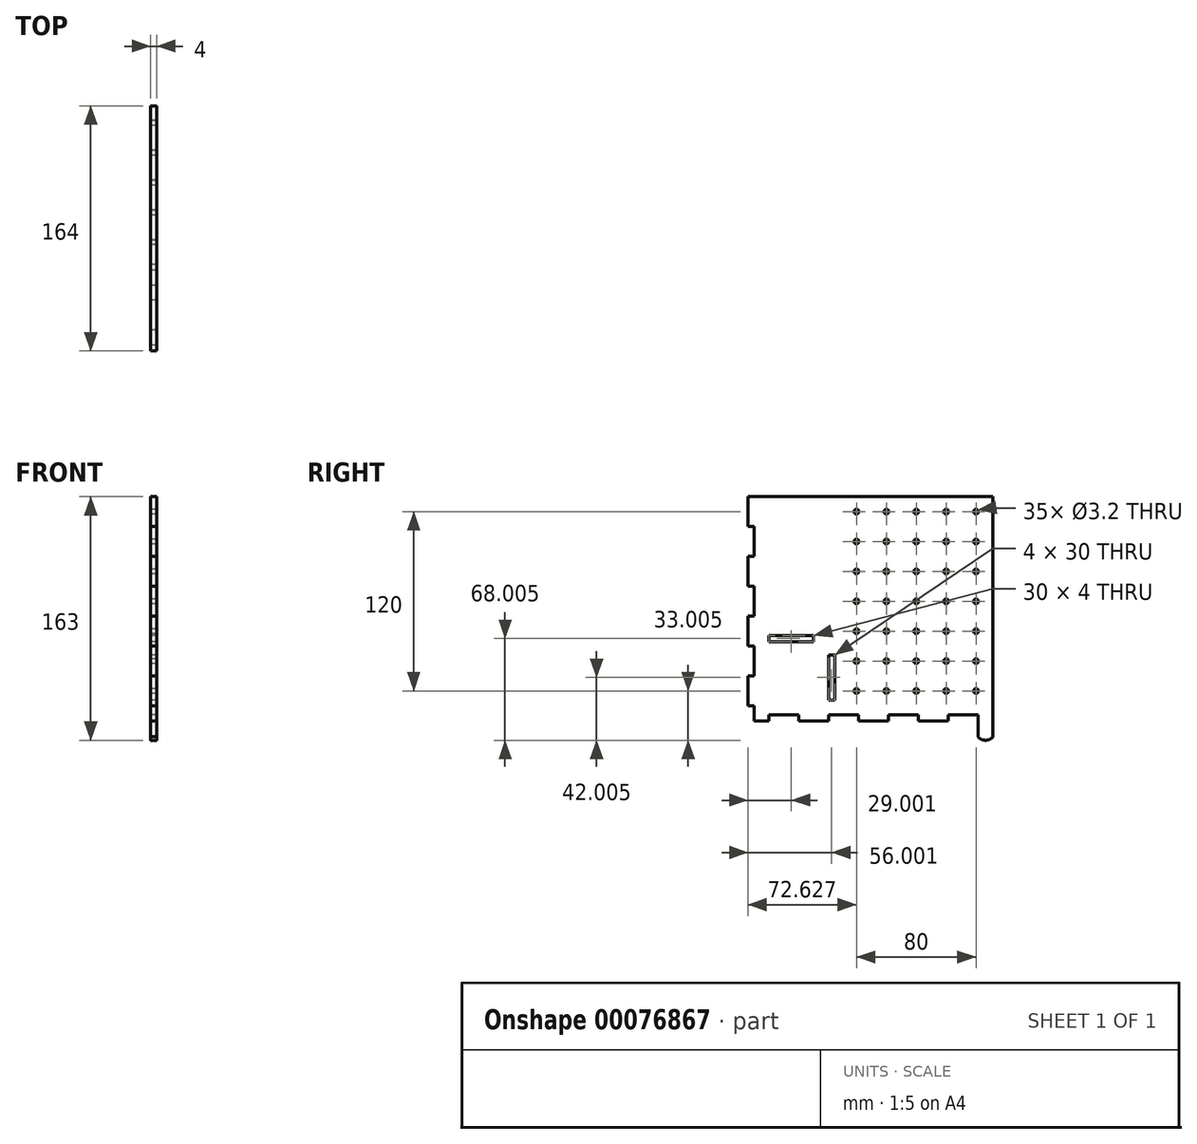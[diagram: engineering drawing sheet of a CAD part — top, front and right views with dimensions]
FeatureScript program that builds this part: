
annotation { "Feature Type Name" : "Feature", "Feature Type Description" : "" }
export const myFeature = defineFeature(function(context is Context, id is Id, definition is map)
    precondition{}
    {
        {
            var Q0;
            Q0=qCreatedBy(makeId("Right.planeOp"),FACE);
            var sketch = newSketch(context, id + "F0", { "sketchPlane" : qUnion([Q0])});
            skLineSegment(sketch, "E0.bottom", {"start": v(-129.98, 84.83) * mm, "end": v(30.02, 84.83) * mm, "construction": true});
            skLineSegment(sketch, "E0.top", {"start": v(-129.98, -65.17) * mm, "end": v(30.02, -65.17) * mm, "construction": true});
            skLineSegment(sketch, "E0.left", {"start": v(-129.98, 84.83) * mm, "end": v(-129.98, -65.17) * mm, "construction": true});
            skLineSegment(sketch, "E0.right", {"start": v(30.02, 84.83) * mm, "end": v(30.02, -65.17) * mm, "construction": true});
            skLineSegment(sketch, "E1.bottom", {"start": v(-119.98, -61.17) * mm, "end": v(-99.98, -61.17) * mm});
            skLineSegment(sketch, "E1.left", {"start": v(-119.98, -61.17) * mm, "end": v(-119.98, -65.17) * mm});
            skLineSegment(sketch, "E1.right", {"start": v(-99.98, -61.17) * mm, "end": v(-99.98, -65.17) * mm});
            skLineSegment(sketch, "E2.1.0.1", {"start": v(-79.98, -61.17) * mm, "end": v(-59.98, -61.17) * mm});
            skLineSegment(sketch, "E2.1.0.2", {"start": v(-79.98, -61.17) * mm, "end": v(-79.98, -65.17) * mm});
            skLineSegment(sketch, "E2.1.0.3", {"start": v(-59.98, -61.17) * mm, "end": v(-59.98, -65.17) * mm});
            skLineSegment(sketch, "E2.2.0.1", {"start": v(-39.98, -61.17) * mm, "end": v(-19.98, -61.17) * mm});
            skLineSegment(sketch, "E2.2.0.2", {"start": v(-39.98, -61.17) * mm, "end": v(-39.98, -65.17) * mm});
            skLineSegment(sketch, "E2.2.0.3", {"start": v(-19.98, -61.17) * mm, "end": v(-19.98, -65.17) * mm});
            skLineSegment(sketch, "E2.3.0.1", {"start": v(0.02, -61.17) * mm, "end": v(20.02, -61.17) * mm});
            skLineSegment(sketch, "E2.3.0.2", {"start": v(0.02, -61.17) * mm, "end": v(0.02, -65.17) * mm});
            skLineSegment(sketch, "E2.3.0.3", {"start": v(20.02, -61.17) * mm, "end": v(20.02, -65.17) * mm});
            skLineSegment(sketch, "E2.direction1", {"start": v(-119.98, -65.17) * mm, "end": v(-79.98, -65.17) * mm, "construction": true});
            skLineSegment(sketch, "E3", {"start": v(-129.98, -65.17) * mm, "end": v(-119.98, -65.17) * mm});
            skLineSegment(sketch, "E4", {"start": v(-99.98, -65.17) * mm, "end": v(-79.98, -65.17) * mm});
            skLineSegment(sketch, "E5", {"start": v(-59.98, -65.17) * mm, "end": v(-39.98, -65.17) * mm});
            skLineSegment(sketch, "E6", {"start": v(-19.98, -65.17) * mm, "end": v(0.02, -65.17) * mm});
            skLineSegment(sketch, "E7", {"start": v(-119.98, -61.17) * mm, "end": v(30.02, -61.17) * mm, "construction": true});
            skLineSegment(sketch, "E8.bottom", {"start": v(-129.98, -55.17) * mm, "end": v(-133.98, -55.17) * mm});
            skLineSegment(sketch, "E8.top", {"start": v(-129.98, -35.17) * mm, "end": v(-133.98, -35.17) * mm});
            skLineSegment(sketch, "E8.right", {"start": v(-133.98, -55.17) * mm, "end": v(-133.98, -35.17) * mm});
            skLineSegment(sketch, "E9.0.1.0", {"start": v(-129.98, 4.83) * mm, "end": v(-133.98, 4.83) * mm});
            skLineSegment(sketch, "E9.0.1.1", {"start": v(-133.98, -15.17) * mm, "end": v(-133.98, 4.83) * mm});
            skLineSegment(sketch, "E9.0.1.2", {"start": v(-129.98, -15.17) * mm, "end": v(-133.98, -15.17) * mm});
            skLineSegment(sketch, "E9.0.2.0", {"start": v(-129.98, 44.83) * mm, "end": v(-133.98, 44.83) * mm});
            skLineSegment(sketch, "E9.0.2.1", {"start": v(-133.98, 24.83) * mm, "end": v(-133.98, 44.83) * mm});
            skLineSegment(sketch, "E9.0.2.2", {"start": v(-129.98, 24.83) * mm, "end": v(-133.98, 24.83) * mm});
            skLineSegment(sketch, "E9.0.3.0", {"start": v(-129.98, 84.83) * mm, "end": v(-133.98, 84.83) * mm});
            skLineSegment(sketch, "E9.0.3.1", {"start": v(-133.98, 64.83) * mm, "end": v(-133.98, 84.83) * mm});
            skLineSegment(sketch, "E9.0.3.2", {"start": v(-129.98, 64.83) * mm, "end": v(-133.98, 64.83) * mm});
            skLineSegment(sketch, "E9.direction2", {"start": v(-133.98, -35.17) * mm, "end": v(-133.98, 4.83) * mm, "construction": true});
            skLineSegment(sketch, "E10", {"start": v(-129.98, 64.83) * mm, "end": v(-129.98, 44.83) * mm});
            skLineSegment(sketch, "E11", {"start": v(-129.98, 24.83) * mm, "end": v(-129.98, 4.83) * mm});
            skLineSegment(sketch, "E12", {"start": v(-129.98, -15.17) * mm, "end": v(-129.98, -35.17) * mm});
            skLineSegment(sketch, "E13", {"start": v(-129.98, -55.17) * mm, "end": v(-129.98, -65.17) * mm});
            skLineSegment(sketch, "E14", {"start": v(-119.98, -61.17) * mm, "end": v(-129.98, -61.17) * mm, "construction": true});
            skLineSegment(sketch, "E15", {"start": v(-129.98, 84.83) * mm, "end": v(30.02, 84.83) * mm});
            skLineSegment(sketch, "E16", {"start": v(30.02, 84.83) * mm, "end": v(30.02, -61.17) * mm});
            skPoint(sketch, "E17", {"position": v(18.65, 74.83) * mm});
            skCircle(sketch, "E18", {"center": v(18.65, 74.83) * mm, "radius": 1.6 * mm});
            skCircle(sketch, "E19.0.1.0", {"center": v(18.65, 54.83) * mm, "radius": 1.6 * mm});
            skPoint(sketch, "E19.0.1.1", {"position": v(18.65, 54.83) * mm});
            skCircle(sketch, "E19.0.2.0", {"center": v(18.65, 34.83) * mm, "radius": 1.6 * mm});
            skPoint(sketch, "E19.0.2.1", {"position": v(18.65, 34.83) * mm});
            skCircle(sketch, "E19.0.3.0", {"center": v(18.65, 14.83) * mm, "radius": 1.6 * mm});
            skPoint(sketch, "E19.0.3.1", {"position": v(18.65, 14.83) * mm});
            skCircle(sketch, "E19.0.4.0", {"center": v(18.65, -5.17) * mm, "radius": 1.6 * mm});
            skPoint(sketch, "E19.0.4.1", {"position": v(18.65, -5.17) * mm});
            skCircle(sketch, "E19.1.0.0", {"center": v(-1.35, 74.83) * mm, "radius": 1.6 * mm});
            skPoint(sketch, "E19.1.0.1", {"position": v(-1.35, 74.83) * mm});
            skCircle(sketch, "E19.1.1.0", {"center": v(-1.35, 54.83) * mm, "radius": 1.6 * mm});
            skPoint(sketch, "E19.1.1.1", {"position": v(-1.35, 54.83) * mm});
            skCircle(sketch, "E19.1.2.0", {"center": v(-1.35, 34.83) * mm, "radius": 1.6 * mm});
            skPoint(sketch, "E19.1.2.1", {"position": v(-1.35, 34.83) * mm});
            skCircle(sketch, "E19.1.3.0", {"center": v(-1.35, 14.83) * mm, "radius": 1.6 * mm});
            skPoint(sketch, "E19.1.3.1", {"position": v(-1.35, 14.83) * mm});
            skCircle(sketch, "E19.1.4.0", {"center": v(-1.35, -5.17) * mm, "radius": 1.6 * mm});
            skPoint(sketch, "E19.1.4.1", {"position": v(-1.35, -5.17) * mm});
            skCircle(sketch, "E19.2.0.0", {"center": v(-21.35, 74.83) * mm, "radius": 1.6 * mm});
            skPoint(sketch, "E19.2.0.1", {"position": v(-21.35, 74.83) * mm});
            skCircle(sketch, "E19.2.1.0", {"center": v(-21.35, 54.83) * mm, "radius": 1.6 * mm});
            skPoint(sketch, "E19.2.1.1", {"position": v(-21.35, 54.83) * mm});
            skCircle(sketch, "E19.2.2.0", {"center": v(-21.35, 34.83) * mm, "radius": 1.6 * mm});
            skPoint(sketch, "E19.2.2.1", {"position": v(-21.35, 34.83) * mm});
            skCircle(sketch, "E19.2.3.0", {"center": v(-21.35, 14.83) * mm, "radius": 1.6 * mm});
            skPoint(sketch, "E19.2.3.1", {"position": v(-21.35, 14.83) * mm});
            skCircle(sketch, "E19.2.4.0", {"center": v(-21.35, -5.17) * mm, "radius": 1.6 * mm});
            skPoint(sketch, "E19.2.4.1", {"position": v(-21.35, -5.17) * mm});
            skCircle(sketch, "E19.3.0.0", {"center": v(-41.35, 74.83) * mm, "radius": 1.6 * mm});
            skPoint(sketch, "E19.3.0.1", {"position": v(-41.35, 74.83) * mm});
            skCircle(sketch, "E19.3.1.0", {"center": v(-41.35, 54.83) * mm, "radius": 1.6 * mm});
            skPoint(sketch, "E19.3.1.1", {"position": v(-41.35, 54.83) * mm});
            skCircle(sketch, "E19.3.2.0", {"center": v(-41.35, 34.83) * mm, "radius": 1.6 * mm});
            skPoint(sketch, "E19.3.2.1", {"position": v(-41.35, 34.83) * mm});
            skCircle(sketch, "E19.3.3.0", {"center": v(-41.35, 14.83) * mm, "radius": 1.6 * mm});
            skPoint(sketch, "E19.3.3.1", {"position": v(-41.35, 14.83) * mm});
            skCircle(sketch, "E19.3.4.0", {"center": v(-41.35, -5.17) * mm, "radius": 1.6 * mm});
            skPoint(sketch, "E19.3.4.1", {"position": v(-41.35, -5.17) * mm});
            skLineSegment(sketch, "E19.direction1", {"start": v(18.65, 74.83) * mm, "end": v(-1.35, 74.83) * mm, "construction": true});
            skLineSegment(sketch, "E19.direction2", {"start": v(18.65, 74.83) * mm, "end": v(18.65, 54.83) * mm, "construction": true});
            skCircle(sketch, "E20.0.0.5", {"center": v(18.65, -25.17) * mm, "radius": 1.6 * mm});
            skPoint(sketch, "E20.2.0.5", {"position": v(18.65, -25.17) * mm});
            skCircle(sketch, "E20.0.0.6", {"center": v(18.65, -45.17) * mm, "radius": 1.6 * mm});
            skPoint(sketch, "E20.2.0.6", {"position": v(18.65, -45.17) * mm});
            skCircle(sketch, "E20.0.1.5", {"center": v(-1.35, -25.17) * mm, "radius": 1.6 * mm});
            skPoint(sketch, "E20.2.1.5", {"position": v(-1.35, -25.17) * mm});
            skCircle(sketch, "E20.0.1.6", {"center": v(-1.35, -45.17) * mm, "radius": 1.6 * mm});
            skPoint(sketch, "E20.2.1.6", {"position": v(-1.35, -45.17) * mm});
            skCircle(sketch, "E20.0.2.5", {"center": v(-21.35, -25.17) * mm, "radius": 1.6 * mm});
            skPoint(sketch, "E20.2.2.5", {"position": v(-21.35, -25.17) * mm});
            skCircle(sketch, "E20.0.2.6", {"center": v(-21.35, -45.17) * mm, "radius": 1.6 * mm});
            skPoint(sketch, "E20.2.2.6", {"position": v(-21.35, -45.17) * mm});
            skCircle(sketch, "E20.0.3.5", {"center": v(-41.35, -25.17) * mm, "radius": 1.6 * mm});
            skPoint(sketch, "E20.2.3.5", {"position": v(-41.35, -25.17) * mm});
            skCircle(sketch, "E20.0.3.6", {"center": v(-41.35, -45.17) * mm, "radius": 1.6 * mm});
            skPoint(sketch, "E20.2.3.6", {"position": v(-41.35, -45.17) * mm});
            skCircle(sketch, "E21.0.4.0", {"center": v(-61.35, 74.83) * mm, "radius": 1.6 * mm});
            skPoint(sketch, "E21.2.4.0", {"position": v(-61.35, 74.83) * mm});
            skCircle(sketch, "E21.0.4.1", {"center": v(-61.35, 54.83) * mm, "radius": 1.6 * mm});
            skPoint(sketch, "E21.2.4.1", {"position": v(-61.35, 54.83) * mm});
            skCircle(sketch, "E21.0.4.2", {"center": v(-61.35, 34.83) * mm, "radius": 1.6 * mm});
            skPoint(sketch, "E21.2.4.2", {"position": v(-61.35, 34.83) * mm});
            skCircle(sketch, "E21.0.4.3", {"center": v(-61.35, 14.83) * mm, "radius": 1.6 * mm});
            skPoint(sketch, "E21.2.4.3", {"position": v(-61.35, 14.83) * mm});
            skCircle(sketch, "E21.0.4.4", {"center": v(-61.35, -5.17) * mm, "radius": 1.6 * mm});
            skPoint(sketch, "E21.2.4.4", {"position": v(-61.35, -5.17) * mm});
            skCircle(sketch, "E21.0.4.5", {"center": v(-61.35, -25.17) * mm, "radius": 1.6 * mm});
            skPoint(sketch, "E21.2.4.5", {"position": v(-61.35, -25.17) * mm});
            skCircle(sketch, "E21.0.4.6", {"center": v(-61.35, -45.17) * mm, "radius": 1.6 * mm});
            skPoint(sketch, "E21.2.4.6", {"position": v(-61.35, -45.17) * mm});
            skLineSegment(sketch, "E22", {"start": v(-79.98, -61.17) * mm, "end": v(-79.98, -12.17) * mm, "construction": true});
            skLineSegment(sketch, "E23", {"start": v(-79.98, -12.17) * mm, "end": v(-129.98, -12.17) * mm, "construction": true});
            skLineSegment(sketch, "E24.bottom", {"start": v(-119.98, -12.17) * mm, "end": v(-89.98, -12.17) * mm});
            skLineSegment(sketch, "E24.top", {"start": v(-119.98, -8.17) * mm, "end": v(-89.98, -8.17) * mm});
            skLineSegment(sketch, "E24.left", {"start": v(-119.98, -12.17) * mm, "end": v(-119.98, -8.17) * mm});
            skLineSegment(sketch, "E24.right", {"start": v(-89.98, -12.17) * mm, "end": v(-89.98, -8.17) * mm});
            skLineSegment(sketch, "E25.bottom", {"start": v(-79.98, -51.17) * mm, "end": v(-75.98, -51.17) * mm});
            skLineSegment(sketch, "E25.top", {"start": v(-79.98, -21.17) * mm, "end": v(-75.98, -21.17) * mm});
            skLineSegment(sketch, "E25.left", {"start": v(-79.98, -51.17) * mm, "end": v(-79.98, -21.17) * mm});
            skLineSegment(sketch, "E25.right", {"start": v(-75.98, -51.17) * mm, "end": v(-75.98, -21.17) * mm});
            skLineSegment(sketch, "E26", {"start": v(30.02, -65.17) * mm, "end": v(30.02, -61.17) * mm});
            skArc(sketch, "E27", {"start": v(20.02, -75.82) * mm, "mid": v(25.02, -78.17) * mm, "end": v(30.02, -75.82) * mm});
            skLineSegment(sketch, "E28", {"start": v(20.02, -65.17) * mm, "end": v(20.02, -75.82) * mm});
            skLineSegment(sketch, "E29", {"start": v(30.02, -65.17) * mm, "end": v(30.02, -75.82) * mm});
            skSolve(sketch);
        }
        {
            var Q0;
            Q0 = qSketchRegion(id + "F0", true);
            extrude(context, id + "F1", {"entities" : qUnion([Q0]), "depth" : 4 * mm});
        }
    });
